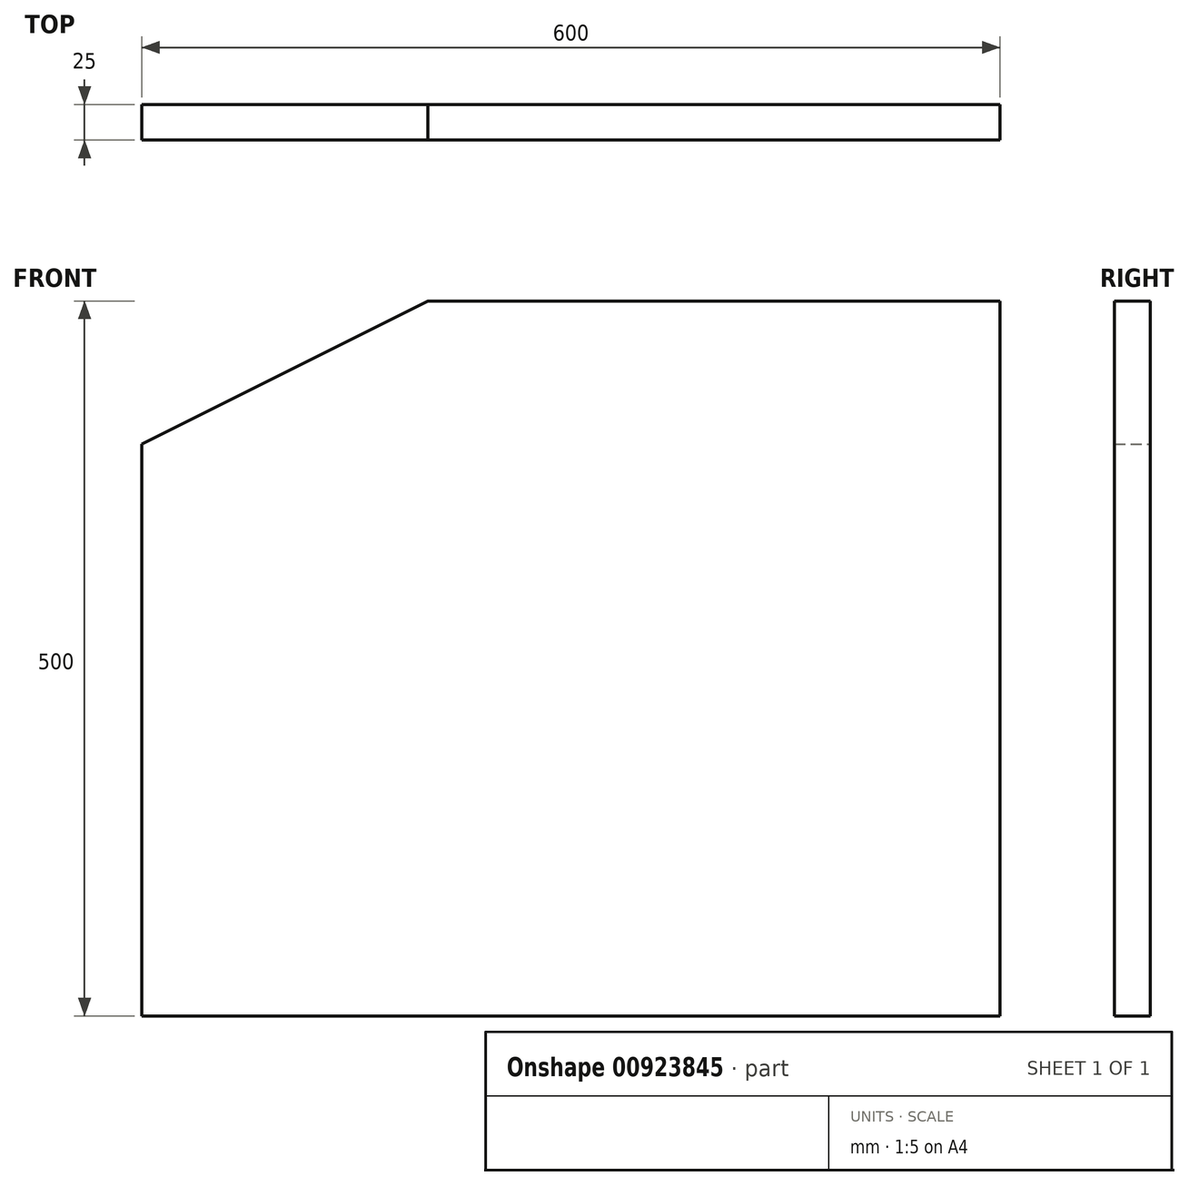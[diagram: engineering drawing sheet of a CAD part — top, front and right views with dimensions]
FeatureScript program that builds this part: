
annotation { "Feature Type Name" : "Feature", "Feature Type Description" : "" }
export const myFeature = defineFeature(function(context is Context, id is Id, definition is map)
    precondition{}
    {
        {
            var Q0;
            Q0=qCreatedBy(makeId("Front.planeOp"),FACE);
            var sketch = newSketch(context, id + "F0", { "sketchPlane" : qUnion([Q0])});
            skLineSegment(sketch, "E0.bottom", {"start": v(24.12, 0) * mm, "end": v(624.12, 0) * mm});
            skLineSegment(sketch, "E0.top", {"start": v(24.12, 500) * mm, "end": v(624.12, 500) * mm});
            skLineSegment(sketch, "E0.left", {"start": v(24.12, 0) * mm, "end": v(24.12, 500) * mm});
            skLineSegment(sketch, "E0.right", {"start": v(624.12, 0) * mm, "end": v(624.12, 500) * mm});
            skLineSegment(sketch, "E1", {"start": v(24.12, 400) * mm, "end": v(224.12, 500) * mm});
            skSolve(sketch);
        }
        {
            var Q0;
            Q0=makeQuery(id+"F0.imprint","IMPRINT",FACE,{"disambiguationData":[TD([[makeQuery(id+"F0.imprint","IMPRINT",EDGE,{"derivedFrom":sQuery(id+"F0.wireOp",EDGE,"E0.bottom")}),1.0]])]});
            extrude(context, id + "F1", {"entities" : qUnion([Q0]), "depth" : 25 * mm, "offsetDistance" : 25 * mm});
        }
    });
